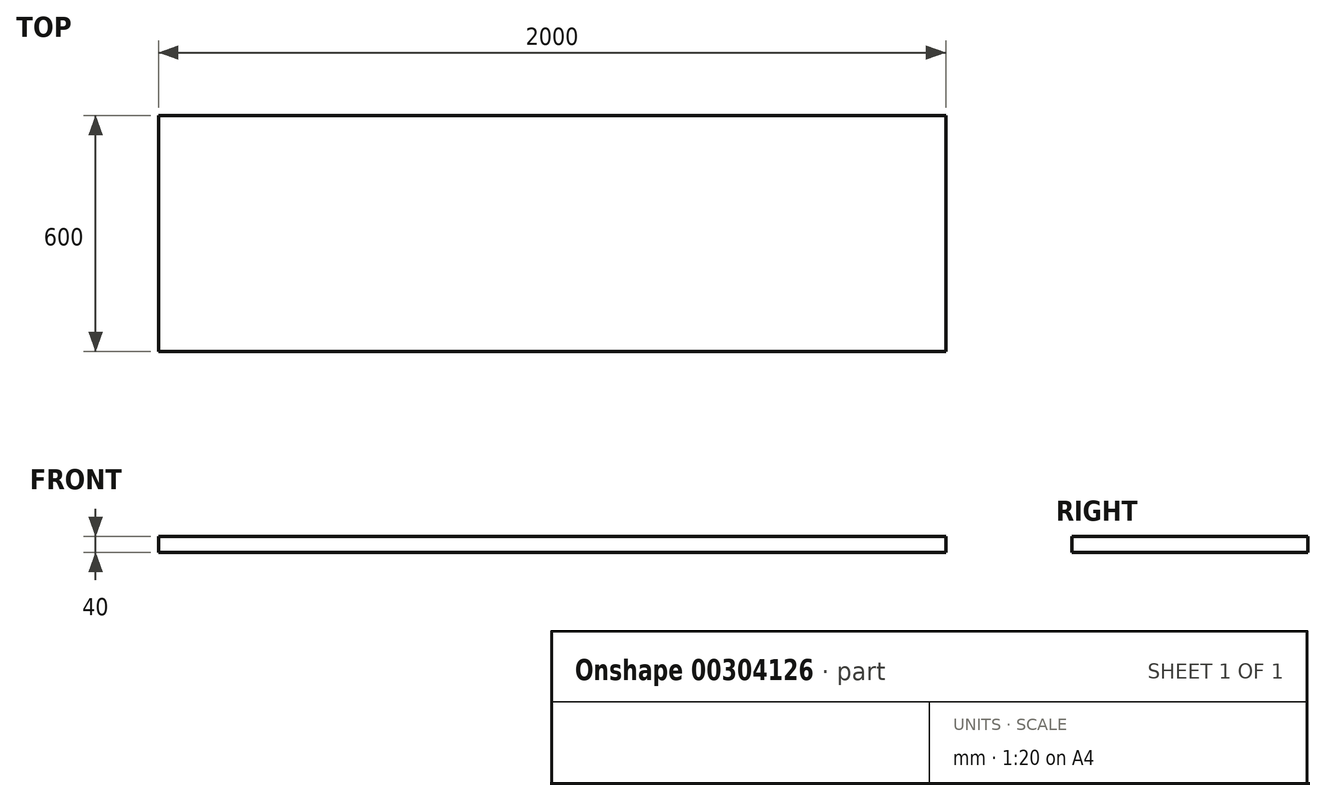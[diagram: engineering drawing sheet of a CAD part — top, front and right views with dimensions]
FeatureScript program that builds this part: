
annotation { "Feature Type Name" : "Feature", "Feature Type Description" : "" }
export const myFeature = defineFeature(function(context is Context, id is Id, definition is map)
    precondition{}
    {
        {
            var Q0;
            Q0=qCreatedBy(makeId("Top.planeOp"),FACE);
            var sketch = newSketch(context, id + "F0", { "sketchPlane" : qUnion([Q0])});
            skLineSegment(sketch, "E0.bottom", {"start": v(-777.3, 305.2) * mm, "end": v(1222.7, 305.2) * mm});
            skLineSegment(sketch, "E0.top", {"start": v(-777.3, -294.8) * mm, "end": v(1222.7, -294.8) * mm});
            skLineSegment(sketch, "E0.left", {"start": v(-777.3, 305.2) * mm, "end": v(-777.3, -294.8) * mm});
            skLineSegment(sketch, "E0.right", {"start": v(1222.7, 305.2) * mm, "end": v(1222.7, -294.8) * mm});
            skSolve(sketch);
        }
        {
            var Q0;
            Q0=makeQuery(id+"F0.imprint","IMPRINT",FACE,{"disambiguationData":[TD([[makeQuery(id+"F0.imprint","IMPRINT",EDGE,{"derivedFrom":sQuery(id+"F0.wireOp",EDGE,"E0.bottom")}),-1.0]])]});
            extrude(context, id + "F1", {"entities" : qUnion([Q0]), "depth" : 40 * mm, "offsetDistance" : 25 * mm});
        }
    });
